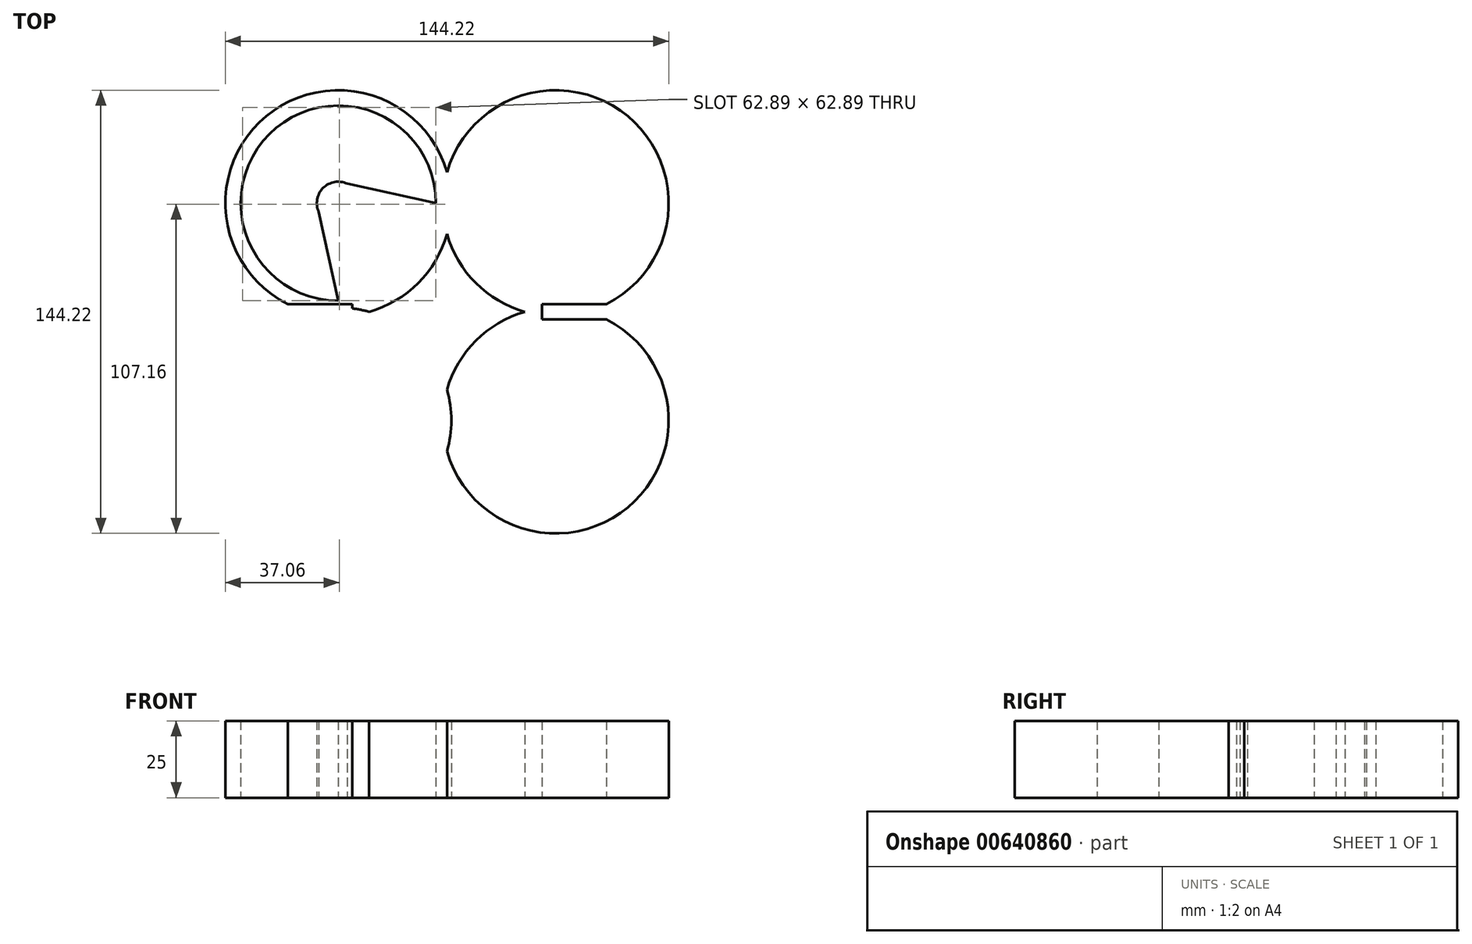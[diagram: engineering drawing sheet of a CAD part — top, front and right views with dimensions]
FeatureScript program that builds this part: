
annotation { "Feature Type Name" : "Feature", "Feature Type Description" : "" }
export const myFeature = defineFeature(function(context is Context, id is Id, definition is map)
    precondition{}
    {
        {
            var Q0;
            Q0=qCreatedBy(makeId("Top.planeOp"),FACE);
            var sketch = newSketch(context, id + "F0", { "sketchPlane" : qUnion([Q0])});
            skCircle(sketch, "E0", {"center": v(-14.14, 0) * mm, "radius": 1.5 * mm});
            skCircle(sketch, "E1", {"center": v(0, 14.14) * mm, "radius": 1.5 * mm});
            skCircle(sketch, "E2", {"center": v(0, -14.14) * mm, "radius": 1.5 * mm});
            skCircle(sketch, "E3", {"center": v(14.14, 0) * mm, "radius": 1.5 * mm});
            skCircle(sketch, "E4", {"center": v(0, 0) * mm, "radius": 6.4 * mm});
            skArc(sketch, "E5", {"start": v(-14.19, 2.5) * mm, "mid": v(-16.64, 0) * mm, "end": v(-14.19, -2.5) * mm});
            skFitSpline(sketch, "E6", {"points": [v(-12.25, 7.75) * mm, v(-11.8, 6.04) * mm, v(-13.24, 2.52) * mm, v(-14.19, 2.5) * mm]});
            skArc(sketch, "E7", {"start": v(2.5, 14.19) * mm, "mid": v(0, 16.64) * mm, "end": v(-2.5, 14.19) * mm});
            skArc(sketch, "E8", {"start": v(-2.5, -14.19) * mm, "mid": v(0, -16.64) * mm, "end": v(2.5, -14.19) * mm});
            skArc(sketch, "E9", {"start": v(14.19, -2.5) * mm, "mid": v(16.64, 0) * mm, "end": v(14.19, 2.5) * mm});
            skFitSpline(sketch, "E10", {"points": [v(-7.75, 12.25) * mm, v(-6.04, 11.8) * mm, v(-2.52, 13.24) * mm, v(-2.5, 14.19) * mm]});
            skFitSpline(sketch, "E11", {"points": [v(12.25, 7.75) * mm, v(11.8, 6.04) * mm, v(13.24, 2.52) * mm, v(14.19, 2.5) * mm]});
            skFitSpline(sketch, "E12", {"points": [v(7.75, 12.25) * mm, v(6.04, 11.8) * mm, v(2.52, 13.24) * mm, v(2.5, 14.19) * mm]});
            skFitSpline(sketch, "E13", {"points": [v(-12.25, -7.75) * mm, v(-11.8, -6.04) * mm, v(-13.24, -2.52) * mm, v(-14.19, -2.5) * mm]});
            skFitSpline(sketch, "E14", {"points": [v(-7.75, -12.25) * mm, v(-6.04, -11.8) * mm, v(-2.52, -13.24) * mm, v(-2.5, -14.19) * mm]});
            skFitSpline(sketch, "E15", {"points": [v(12.25, -7.75) * mm, v(11.8, -6.04) * mm, v(13.24, -2.52) * mm, v(14.19, -2.5) * mm]});
            skFitSpline(sketch, "E16", {"points": [v(7.75, -12.25) * mm, v(6.04, -11.8) * mm, v(2.52, -13.24) * mm, v(2.5, -14.19) * mm]});
            skCircle(sketch, "E17", {"center": v(-30.86, -35.36) * mm, "radius": 1 * mm});
            skCircle(sketch, "E18", {"center": v(-35.36, -39.86) * mm, "radius": 1 * mm});
            skCircle(sketch, "E19", {"center": v(-39.86, -35.36) * mm, "radius": 1 * mm});
            skCircle(sketch, "E20", {"center": v(-35.36, -30.86) * mm, "radius": 1 * mm});
            skLineSegment(sketch, "E21", {"start": v(-7.75, -12.25) * mm, "end": v(-10.77, -15.27) * mm});
            skLineSegment(sketch, "E22", {"start": v(-12.25, -7.75) * mm, "end": v(-15.27, -10.77) * mm});
            skLineSegment(sketch, "E23", {"start": v(-35.36, -3.6) * mm, "end": v(-41.71, -32.43) * mm});
            skLineSegment(sketch, "E24", {"start": v(-31.5, -7.4) * mm, "end": v(-35.36, -28.36) * mm});
            skLineSegment(sketch, "E25", {"start": v(-8.1, -31.72) * mm, "end": v(-28.38, -35.9) * mm});
            skArc(sketch, "E26", {"start": v(-41.71, -32.43) * mm, "mid": v(-40.3, -40.3) * mm, "end": v(-32.43, -41.71) * mm});
            skArc(sketch, "E27", {"start": v(-28.38, -35.9) * mm, "mid": v(-30.21, -30.6) * mm, "end": v(-35.36, -28.36) * mm});
            skArc(sketch, "E28", {"start": v(-8.1, -31.72) * mm, "mid": v(-15.3, -15.23) * mm, "end": v(-31.5, -7.4) * mm});
            skArc(sketch, "E29", {"start": v(-3.93, -30.86) * mm, "mid": v(-6.28, -22.6) * mm, "end": v(-10.77, -15.27) * mm});
            skArc(sketch, "E30", {"start": v(-15.27, -10.77) * mm, "mid": v(-22.6, -6.28) * mm, "end": v(-30.86, -3.93) * mm});
            skLineSegment(sketch, "E31", {"start": v(10.77, 15.27) * mm, "end": v(7.75, 12.25) * mm});
            skLineSegment(sketch, "E32", {"start": v(15.27, 10.77) * mm, "end": v(12.25, 7.75) * mm});
            skLineSegment(sketch, "E33", {"start": v(-3.6, -35.36) * mm, "end": v(-32.43, -41.71) * mm});
            skCircle(sketch, "E34", {"center": v(35.36, 30.86) * mm, "radius": 1 * mm});
            skCircle(sketch, "E35", {"center": v(39.86, 35.36) * mm, "radius": 1 * mm});
            skCircle(sketch, "E36", {"center": v(35.36, 39.86) * mm, "radius": 1 * mm});
            skCircle(sketch, "E37", {"center": v(30.86, 35.36) * mm, "radius": 1 * mm});
            skLineSegment(sketch, "E38", {"start": v(12.25, 7.75) * mm, "end": v(15.27, 10.77) * mm});
            skLineSegment(sketch, "E39", {"start": v(7.75, 12.25) * mm, "end": v(10.77, 15.27) * mm});
            skLineSegment(sketch, "E40", {"start": v(3.6, 35.36) * mm, "end": v(32.43, 41.71) * mm});
            skLineSegment(sketch, "E41", {"start": v(7.4, 31.5) * mm, "end": v(28.36, 35.36) * mm});
            skLineSegment(sketch, "E42", {"start": v(31.72, 8.1) * mm, "end": v(35.9, 28.38) * mm});
            skArc(sketch, "E43", {"start": v(41.71, 32.43) * mm, "mid": v(40.3, 40.3) * mm, "end": v(32.43, 41.71) * mm});
            skArc(sketch, "E44", {"start": v(28.36, 35.36) * mm, "mid": v(30.6, 30.21) * mm, "end": v(35.9, 28.38) * mm});
            skArc(sketch, "E45", {"start": v(7.4, 31.5) * mm, "mid": v(15.23, 15.3) * mm, "end": v(31.72, 8.1) * mm});
            skArc(sketch, "E46", {"start": v(15.27, 10.77) * mm, "mid": v(22.6, 6.28) * mm, "end": v(30.86, 3.93) * mm});
            skArc(sketch, "E47", {"start": v(3.93, 30.86) * mm, "mid": v(6.28, 22.6) * mm, "end": v(10.77, 15.27) * mm});
            skLineSegment(sketch, "E48", {"start": v(35.36, 3.6) * mm, "end": v(41.71, 32.43) * mm});
            skCircle(sketch, "E49", {"center": v(30.86, -35.36) * mm, "radius": 1 * mm});
            skCircle(sketch, "E50", {"center": v(35.36, -39.86) * mm, "radius": 1 * mm});
            skCircle(sketch, "E51", {"center": v(39.86, -35.36) * mm, "radius": 1 * mm});
            skCircle(sketch, "E52", {"center": v(35.36, -30.86) * mm, "radius": 1 * mm});
            skLineSegment(sketch, "E53", {"start": v(7.75, -12.25) * mm, "end": v(10.77, -15.27) * mm});
            skLineSegment(sketch, "E54", {"start": v(12.25, -7.75) * mm, "end": v(15.27, -10.77) * mm});
            skLineSegment(sketch, "E55", {"start": v(35.36, -3.6) * mm, "end": v(41.71, -32.43) * mm});
            skLineSegment(sketch, "E56", {"start": v(31.5, -7.4) * mm, "end": v(35.36, -28.36) * mm});
            skLineSegment(sketch, "E57", {"start": v(8.1, -31.72) * mm, "end": v(28.38, -35.9) * mm});
            skArc(sketch, "E58", {"start": v(32.43, -41.71) * mm, "mid": v(40.3, -40.3) * mm, "end": v(41.71, -32.43) * mm});
            skArc(sketch, "E59", {"start": v(35.36, -28.36) * mm, "mid": v(30.21, -30.6) * mm, "end": v(28.38, -35.9) * mm});
            skArc(sketch, "E60", {"start": v(31.5, -7.4) * mm, "mid": v(15.3, -15.23) * mm, "end": v(8.1, -31.72) * mm});
            skArc(sketch, "E61", {"start": v(10.77, -15.27) * mm, "mid": v(6.28, -22.6) * mm, "end": v(3.93, -30.86) * mm});
            skArc(sketch, "E62", {"start": v(30.86, -3.93) * mm, "mid": v(22.6, -6.28) * mm, "end": v(15.27, -10.77) * mm});
            skLineSegment(sketch, "E63", {"start": v(3.6, -35.36) * mm, "end": v(32.43, -41.71) * mm});
            skCircle(sketch, "E64", {"center": v(-35.36, 30.86) * mm, "radius": 1 * mm});
            skCircle(sketch, "E65", {"center": v(-39.86, 35.36) * mm, "radius": 1 * mm});
            skCircle(sketch, "E66", {"center": v(-35.36, 39.86) * mm, "radius": 1 * mm});
            skCircle(sketch, "E67", {"center": v(-30.86, 35.36) * mm, "radius": 1 * mm});
            skLineSegment(sketch, "E68", {"start": v(-12.25, 7.75) * mm, "end": v(-15.27, 10.77) * mm});
            skLineSegment(sketch, "E69", {"start": v(-7.75, 12.25) * mm, "end": v(-10.77, 15.27) * mm});
            skLineSegment(sketch, "E70", {"start": v(-3.6, 35.36) * mm, "end": v(-32.43, 41.71) * mm});
            skLineSegment(sketch, "E71", {"start": v(-7.4, 31.5) * mm, "end": v(-28.36, 35.36) * mm});
            skLineSegment(sketch, "E72", {"start": v(-31.72, 8.1) * mm, "end": v(-35.9, 28.38) * mm});
            skArc(sketch, "E73", {"start": v(-35.9, 28.38) * mm, "mid": v(-30.6, 30.21) * mm, "end": v(-28.36, 35.36) * mm});
            skArc(sketch, "E74", {"start": v(-32.43, 41.71) * mm, "mid": v(-40.3, 40.3) * mm, "end": v(-41.71, 32.43) * mm});
            skArc(sketch, "E75", {"start": v(-31.72, 8.1) * mm, "mid": v(-15.23, 15.3) * mm, "end": v(-7.4, 31.5) * mm});
            skArc(sketch, "E76", {"start": v(-30.86, 3.93) * mm, "mid": v(-22.6, 6.28) * mm, "end": v(-15.27, 10.77) * mm});
            skArc(sketch, "E77", {"start": v(-10.77, 15.27) * mm, "mid": v(-6.28, 22.6) * mm, "end": v(-3.93, 30.86) * mm});
            skLineSegment(sketch, "E78", {"start": v(-35.36, 3.6) * mm, "end": v(-41.71, 32.43) * mm});
            skLineSegment(sketch, "E79", {"start": v(-35.36, -3.6) * mm, "end": v(-35.36, 3.6) * mm});
            skLineSegment(sketch, "E80", {"start": v(-30.86, -3.93) * mm, "end": v(-30.86, 3.93) * mm});
            skLineSegment(sketch, "E81", {"start": v(3.6, 35.36) * mm, "end": v(-3.6, 35.36) * mm});
            skLineSegment(sketch, "E82", {"start": v(3.93, 30.86) * mm, "end": v(-3.93, 30.86) * mm});
            skLineSegment(sketch, "E83", {"start": v(-3.6, -35.36) * mm, "end": v(3.6, -35.36) * mm});
            skLineSegment(sketch, "E84", {"start": v(-3.93, -30.86) * mm, "end": v(3.93, -30.86) * mm});
            skLineSegment(sketch, "E85", {"start": v(35.36, 3.6) * mm, "end": v(35.36, -3.6) * mm});
            skLineSegment(sketch, "E86", {"start": v(30.86, 3.93) * mm, "end": v(30.86, -3.93) * mm});
            skCircle(sketch, "E87", {"center": v(0, 32.86) * mm, "radius": 1 * mm});
            skCircle(sketch, "E88", {"center": v(32.86, 0) * mm, "radius": 1 * mm});
            skCircle(sketch, "E89", {"center": v(-32.86, 0) * mm, "radius": 1 * mm});
            skCircle(sketch, "E90", {"center": v(0, -32.86) * mm, "radius": 1 * mm});
            skCircle(sketch, "E91", {"center": v(-8, 8) * mm, "radius": 1.5 * mm});
            skCircle(sketch, "E92", {"center": v(8, 8) * mm, "radius": 1.5 * mm});
            skCircle(sketch, "E93", {"center": v(-8, -8) * mm, "radius": 1.5 * mm});
            skCircle(sketch, "E94", {"center": v(8, -8) * mm, "radius": 1.5 * mm});
            skCircle(sketch, "E95", {"center": v(-35.36, 35.36) * mm, "radius": 2.25 * mm});
            skCircle(sketch, "E96", {"center": v(35.36, 35.36) * mm, "radius": 2.25 * mm});
            skCircle(sketch, "E97", {"center": v(-35.36, -35.36) * mm, "radius": 2.25 * mm});
            skCircle(sketch, "E98", {"center": v(35.36, -35.36) * mm, "radius": 2.25 * mm});
            skCircle(sketch, "E99", {"center": v(-35.36, 35.36) * mm, "radius": 31.75 * mm});
            skCircle(sketch, "E100", {"center": v(35.36, 35.36) * mm, "radius": 31.75 * mm});
            skCircle(sketch, "E101", {"center": v(-35.36, -35.36) * mm, "radius": 31.75 * mm});
            skCircle(sketch, "E102", {"center": v(35.36, -35.36) * mm, "radius": 31.75 * mm});
            skSolve(sketch);
        }
        {
            var Q0;
            {var subQ0=sQuery(id+"F0.wireOp",EDGE,"E70");Q0=makeQuery(id+"F0.imprint","IMPRINT",FACE,{"disambiguationData":[TD([[makeQuery(id+"F0.imprint","IMPRINT",EDGE,{"derivedFrom":subQ0}),-1.0]])]});}
            var sketch = newSketch(context, id + "F1", { "sketchPlane" : qUnion([Q0])});
            skPoint(sketch, "E103.0", {"position": v(-35.36, 35.36) * mm});
            skPoint(sketch, "E104.0", {"position": v(35.36, 35.36) * mm});
            skPoint(sketch, "E105.0", {"position": v(35.36, -35.36) * mm});
            skPoint(sketch, "E106.0", {"position": v(-35.36, -35.36) * mm});
            skArc(sketch, "E107", {"start": v(-30.86, -1.12) * mm, "mid": v(-9.37, 9.37) * mm, "end": v(1.12, 30.86) * mm});
            skCircle(sketch, "E108.0", {"center": v(-35.36, 35.36) * mm, "radius": 31.75 * mm, "construction": true});
            skCircle(sketch, "E109.0", {"center": v(35.36, 35.36) * mm, "radius": 31.75 * mm, "construction": true});
            skCircle(sketch, "E110.0", {"center": v(35.36, -35.36) * mm, "radius": 31.75 * mm, "construction": true});
            skCircle(sketch, "E111.0", {"center": v(-35.36, -35.36) * mm, "radius": 31.75 * mm, "construction": true});
            skLineSegment(sketch, "E112.0.0", {"start": v(-35.36, 3.6) * mm, "end": v(-35.36, -3.6) * mm, "construction": true});
            skArc(sketch, "E112.0.1", {"start": v(-35.36, -3.6) * mm, "mid": v(-33.1, -3.69) * mm, "end": v(-30.86, -3.93) * mm, "construction": true});
            skLineSegment(sketch, "E112.0.2", {"start": v(-30.86, -3.93) * mm, "end": v(-30.86, 3.93) * mm, "construction": true});
            skArc(sketch, "E112.0.3", {"start": v(-30.86, 3.93) * mm, "mid": v(-33.1, 3.69) * mm, "end": v(-35.36, 3.6) * mm, "construction": true});
            skLineSegment(sketch, "E113.0.0", {"start": v(3.93, -30.86) * mm, "end": v(-3.93, -30.86) * mm, "construction": true});
            skArc(sketch, "E113.0.1", {"start": v(-3.93, -30.86) * mm, "mid": v(-3.69, -33.1) * mm, "end": v(-3.6, -35.36) * mm, "construction": true});
            skLineSegment(sketch, "E113.0.2", {"start": v(-3.6, -35.36) * mm, "end": v(3.6, -35.36) * mm, "construction": true});
            skArc(sketch, "E113.0.3", {"start": v(3.6, -35.36) * mm, "mid": v(3.69, -33.1) * mm, "end": v(3.93, -30.86) * mm, "construction": true});
            skLineSegment(sketch, "E114.0.0", {"start": v(35.36, -3.6) * mm, "end": v(35.36, 3.6) * mm, "construction": true});
            skArc(sketch, "E114.0.1", {"start": v(35.36, 3.6) * mm, "mid": v(33.1, 3.69) * mm, "end": v(30.86, 3.93) * mm, "construction": true});
            skLineSegment(sketch, "E114.0.2", {"start": v(30.86, 3.93) * mm, "end": v(30.86, -3.93) * mm, "construction": true});
            skArc(sketch, "E114.0.3", {"start": v(30.86, -3.93) * mm, "mid": v(33.1, -3.69) * mm, "end": v(35.36, -3.6) * mm, "construction": true});
            skLineSegment(sketch, "E115.0.0", {"start": v(-3.93, 30.86) * mm, "end": v(3.93, 30.86) * mm, "construction": true});
            skArc(sketch, "E115.0.1", {"start": v(3.93, 30.86) * mm, "mid": v(3.69, 33.1) * mm, "end": v(3.6, 35.36) * mm, "construction": true});
            skLineSegment(sketch, "E115.0.2", {"start": v(3.6, 35.36) * mm, "end": v(-3.6, 35.36) * mm, "construction": true});
            skArc(sketch, "E115.0.3", {"start": v(-3.6, 35.36) * mm, "mid": v(-3.69, 33.1) * mm, "end": v(-3.93, 30.86) * mm, "construction": true});
            skArc(sketch, "E116", {"start": v(-1.12, 30.86) * mm, "mid": v(7.45, 11.44) * mm, "end": v(25.33, 0) * mm});
            skArc(sketch, "E117", {"start": v(-45.38, 0) * mm, "mid": v(-32.54, -72) * mm, "end": v(-30.86, 1.12) * mm});
            skLineSegment(sketch, "E118.bottom", {"start": v(51.82, 2.5) * mm, "end": v(-51.82, 2.5) * mm, "construction": true});
            skLineSegment(sketch, "E118.top", {"start": v(51.82, -2.5) * mm, "end": v(-51.82, -2.5) * mm, "construction": true});
            skLineSegment(sketch, "E118.left", {"start": v(51.82, 2.5) * mm, "end": v(51.82, -2.5) * mm, "construction": true});
            skLineSegment(sketch, "E118.right", {"start": v(-51.82, 2.5) * mm, "end": v(-51.82, -2.5) * mm, "construction": true});
            skPoint(sketch, "E118.middle", {"position": v(0, 0) * mm});
            skLineSegment(sketch, "E119", {"start": v(-51.82, 2.5) * mm, "end": v(-30.86, 2.5) * mm});
            skLineSegment(sketch, "E120", {"start": v(-30.86, 2.5) * mm, "end": v(-30.86, -2.5) * mm});
            skLineSegment(sketch, "E121", {"start": v(-30.86, -2.5) * mm, "end": v(-51.82, -2.5) * mm});
            skLineSegment(sketch, "E122", {"start": v(-51.82, 2.5) * mm, "end": v(-51.82, -2.5) * mm});
            skLineSegment(sketch, "E123", {"start": v(51.82, 2.5) * mm, "end": v(51.82, -2.5) * mm});
            skLineSegment(sketch, "E124", {"start": v(30.86, -2.5) * mm, "end": v(30.86, 2.5) * mm});
            skLineSegment(sketch, "E125", {"start": v(30.86, 2.5) * mm, "end": v(51.82, 2.5) * mm});
            skLineSegment(sketch, "E126", {"start": v(51.82, -2.5) * mm, "end": v(30.86, -2.5) * mm});
            skPoint(sketch, "E127.0", {"position": v(-32.86, 0) * mm});
            skCircle(sketch, "E128", {"center": v(-32.86, 0) * mm, "radius": 1.5 * mm});
            skArc(sketch, "E129.trimOffspring", {"start": v(0, 45.38) * mm, "mid": v(-61.34, 61.34) * mm, "end": v(-45.38, 0) * mm});
            skArc(sketch, "E130.trimOffspring", {"start": v(45.38, 0) * mm, "mid": v(61.34, 61.34) * mm, "end": v(0, 45.38) * mm});
            skArc(sketch, "E131.trimOffspring", {"start": v(25.33, 0) * mm, "mid": v(35.36, -72.1) * mm, "end": v(45.38, 0) * mm});
            skSolve(sketch);
        }
        {
            var Q0;
            {var subQ4=sQuery(id+"F1.wireOp",EDGE,"E119");Q0=makeQuery(id+"F1.imprint","IMPRINT",FACE,{"disambiguationData":[TD([[makeQuery(id+"F1.imprint","IMPRINT",EDGE,{"derivedFrom":subQ4}),1.0]])]});}
            extrude(context, id + "F2", {"entities" : qUnion([Q0]), "depth" : 25 * mm, "offsetDistance" : 25 * mm});
        }
    });
